# Revit family: UNB_Specchio_Multiproduct_BIM_IT_T3428;T3430;T3439;T3442;T3498;T3499
name_source: partatom
category: Plumbing Fixtures
revit_build: Autodesk Revit 2017 (Build: 20160225_1515(x64)
units: mm (PartAtom-declared; Revit-internal decimal feet)

## family parameters
Cut with Voids When Loaded = No
Host = Face
Part Type = Normal
Room Calculation Point = No
Round Connector Dimension = Use Diameter
Shared = No

## types (6) — shared parameters
Accessori = http://www.idealstandard.it
AltezzaNominale = 700 mm  [stored 2.29659 ft]
Autore = Ideal Standard
Brand = Ideal Standard
CodiceDiPrestazione = EN
Colore = specchio
Connessione = piombatura
Default Elevation = 1500 mm
DescrizioneClassifcazioneUni2015 = Bathroom furniture
Finitura = specchio
Forma = rettangolare
Garanzia = garanzia del produttore
IfcEsportaCome = BATHROOM FURNITURE
InformazioniDiProdotto = http://www.idealstandard.it
InstruzioniInstallazione = http://www.idealstandard.it
LunghezzaNominale = 170 mm
Materiale = bicchiere
PartiDiRicambio = http://www.idealstandard.it
ProfonditàNominale = 170 mm
Revisione = 1
RiferimentoClassificazioneUni2015 = MIRRORS
Spazio = interno
Telefono = 800 652 290
TipoDiDato = Fisso
TipoEspotazioneIfc = IfcFurnitureType
TipologiaVaso = Altro
URL = http://www.idealstandard.it
UnitàDurata = anno
UnitàDurataGaranzia = anno
UnitàLineare = millimetro
UnitàMonetaria = €
UnitàSuperficie = millimetro
UnitàVolume = litro
Versione = 1
VersioneClassificazioneUni2015 = IfcFurnitureType
zero-valued in all types: Cost, CostoDiSostituzione

## per-type parameters (varying)
| type | Caratteristiche | CodiceABarre | Description | DoubleUnitsOnly | LarghezzaNominale | Model | ModelloDiRiferimento | Nome | NomeOggettoBim | NumeroDiModello | PesoNetto | Riferimento | SingleUnitsOnly |
| T3428 - 500 x 700 mirror cabinets | SPECCHIO CONT. MID 50X70 MATT AL 4W 230W | 8014140447757 | SPECCHIO CONT. MID 50X70 MATT AL 4W 230W | No | 500 mm | T3428AL | SPECCHIO CONT. MID 50X70 MATT AL 4W 230W | ISI_IdealStandard_Specchio_T3428 | ISI_IdealStandard_Specchio_T3428 | T3428AL | 16.00 Kg | T3428 | Yes |
| T3430 - 600 x 700 mirror cabinet | SPECCHIO CONT. MID 60X70 MATT AL 5W 230W | 8014140447771 | SPECCHIO CONT. MID 60X70 MATT AL 5W 230W | No | 600 mm | T3430AL | SPECCHIO CONT. MID 60X70 MATT AL 5W 230W | ISI_IdealStandard_Specchio_T3430 | ISI_IdealStandard_Specchio_T3430 | T3430AL | 18.00 Kg | T3430 | Yes |
| T3439 - 700 x 700 mirror cabinet | SPECCHIO CONT. MID 70X70 MATT AL 6,3W 23 | 8014140447795 | SPECCHIO CONT. MID 70X70 MATT AL 6,3W 23 | Yes | 700 mm  [stored 2.29659 ft] | T3439AL | SPECCHIO CONT. MID 70X70 MATT AL 6,3W 23 | ISI_IdealStandard_Specchio_T3439 | ISI_IdealStandard_Specchio_T3439 | T3439AL | 20.00 Kg | T3439 | No |
| T3442 - 800 x 700 mirror cabinet | SPECCHIO CONT. MID 80X70 MATT AL 7W 230W | 8014140447818 | SPECCHIO CONT. MID 80X70 MATT AL 7W 230W | Yes | 800 mm | T3442AL | SPECCHIO CONT. MID 80X70 MATT AL 7W 230W | ISI_IdealStandard_Specchio_T3442 | ISI_IdealStandard_Specchio_T3442 | T3442AL | 22.00 Kg | T3442 | No |
| T3498 - 1000 x 700 mirror cabinet | SPECCHIO CONT. MID 100X70 MATT AL 9W 230 | 8014140447832 | SPECCHIO CONT. MID 100X70 MATT AL 9W 230 | Yes | 1000 mm | T3498AL | SPECCHIO CONT. MID 100X70 MATT AL 9W 230 | ISI_IdealStandard_Specchio_T3498 | ISI_IdealStandard_Specchio_T3498 | T3498AL | 26.00 Kg | T3498 | No |
| T3499 - 1200 x 700 mirror cabinet | SPECCHIO CONT. MID 120X70 MATT AL 11W 23 | 8014140447856 | SPECCHIO CONT. MID 120X70 MATT AL 11W 23 | Yes | 1200 mm  [stored 3.93701 ft] | T3499AL | SPECCHIO CONT. MID 120X70 MATT AL 11W 23 | ISI_IdealStandard_Specchio_T3499 | ISI_IdealStandard_Specchio_T3499 | T3499AL | 28.00 Kg | T3499 | No |

note: [stored X ft] marks values corroborated as IEEE doubles in the binary element streams (Revit-internal decimal feet)

## geometry (parser evidence)
native form markers: Sweep x2
no freeform markers — native parametric forms only
